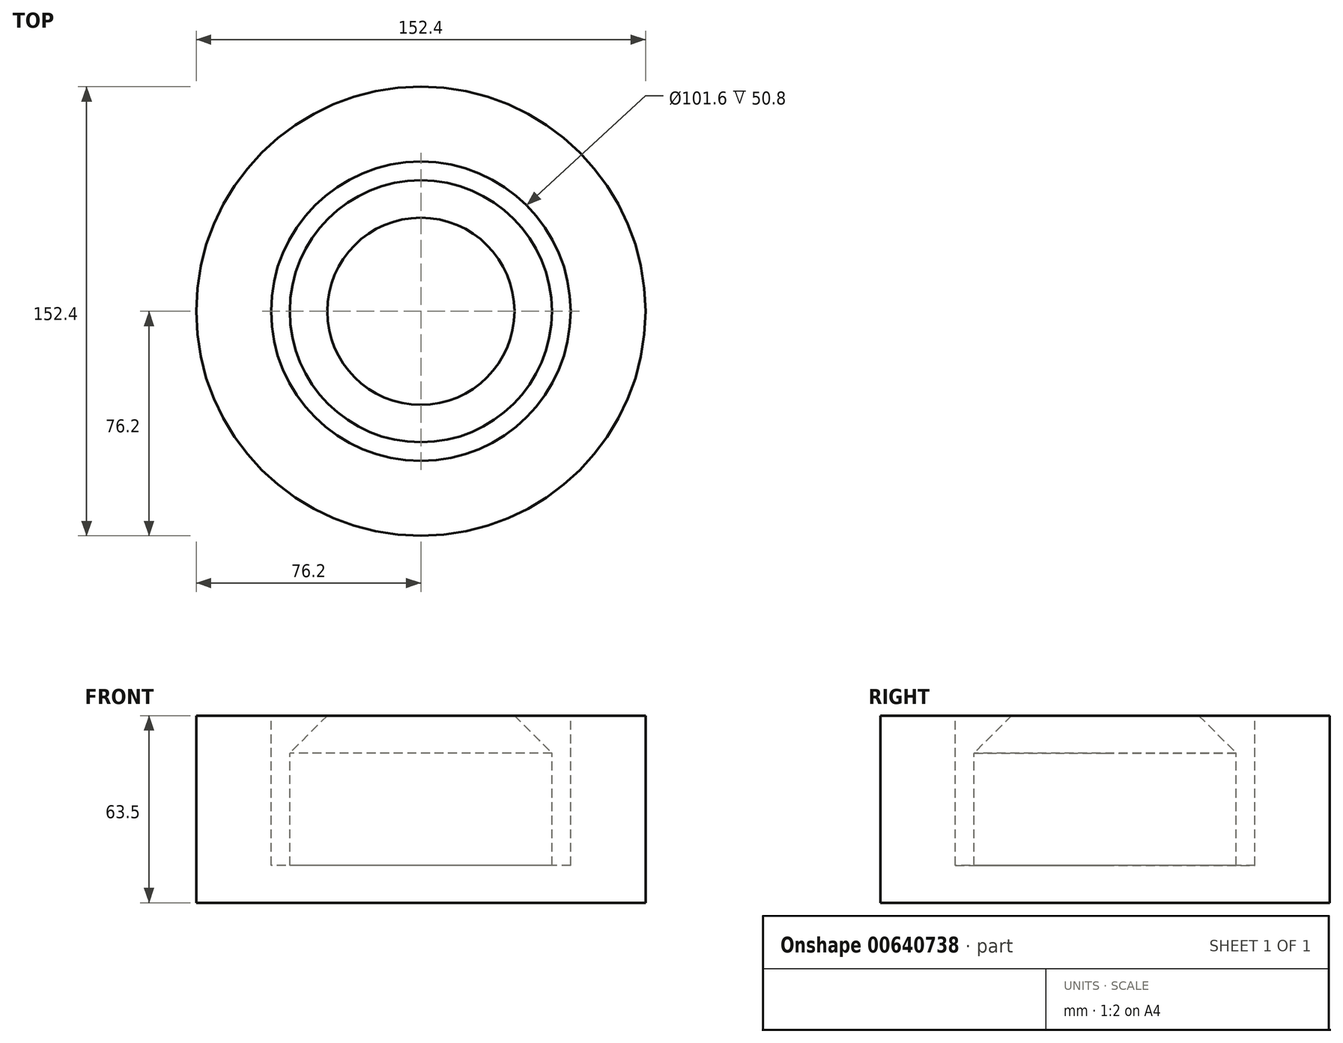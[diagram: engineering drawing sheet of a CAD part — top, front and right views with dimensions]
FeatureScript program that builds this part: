
annotation { "Feature Type Name" : "Feature", "Feature Type Description" : "" }
export const myFeature = defineFeature(function(context is Context, id is Id, definition is map)
    precondition{}
    {
        {
            var Q0;
            Q0=qCreatedBy(makeId("Top.planeOp"),FACE);
            var sketch = newSketch(context, id + "F0", { "sketchPlane" : qUnion([Q0])});
            skCircle(sketch, "E0", {"center": v(0, 0) * mm, "radius": 76.2 * mm});
            skSolve(sketch);
        }
        {
            var Q0;
            Q0=makeQuery(id+"F0.imprint","IMPRINT",FACE,{"disambiguationData":[TD([[makeQuery(id+"F0.imprint","IMPRINT",EDGE,{"derivedFrom":sQuery(id+"F0.wireOp",EDGE,"E0")}),1.0]])]});
            extrude(context, id + "F1", {"entities" : qUnion([Q0]), "depth" : 63.5 * mm, "offsetDistance" : 25 * mm});
        }
        {
            var Q0;
            Q0=makeQuery(id+"F1.opExtrude","CAP_FACE",FACE,{"disambiguationData":[OSD([sQuery(id+"F0.wireOp",EDGE,"E0")])],"isStart":false});
            var sketch = newSketch(context, id + "F2", { "sketchPlane" : qUnion([Q0])});
            skCircle(sketch, "E1", {"center": v(0, 0) * mm, "radius": 44.45 * mm});
            skCircle(sketch, "E2", {"center": v(0, 0) * mm, "radius": 50.8 * mm});
            skSolve(sketch);
        }
        {
            var Q0;
            Q0=makeQuery(id+"F2.imprint","IMPRINT",FACE,{"disambiguationData":[TD([[makeQuery(id+"F2.imprint","IMPRINT",EDGE,{"derivedFrom":sQuery(id+"F2.wireOp",EDGE,"E1")}),-1.0]])]});
            extrude(context, id + "F3", {"entities" : qUnion([Q0]), "operationType" : NewBodyOperationType.REMOVE, "oppositeDirection" : true, "depth" : 50.8 * mm, "offsetDistance" : 25 * mm});
        }
        {
            var Q0;
            Q0=makeQuery(id+"F3.boolean.opBoolean","COPY",EDGE,{"derivedFrom":makeQuery(id+"F3.opExtrude","CAP_EDGE",EDGE,{"disambiguationData":[OSD([sQuery(id+"F2.wireOp",EDGE,"E2")])],"isStart":true})});
            var Q1;
            Q1=makeQuery(id+"F3.boolean.opBoolean","COPY",EDGE,{"derivedFrom":makeQuery(id+"F3.opExtrude","CAP_EDGE",EDGE,{"disambiguationData":[OSD([sQuery(id+"F2.wireOp",EDGE,"E1")])],"isStart":true})});
            chamfer(context, id + "F4", {"entities" : qUnion([Q0, Q1]), "width" : 12.7 * mm});
        }
    });
